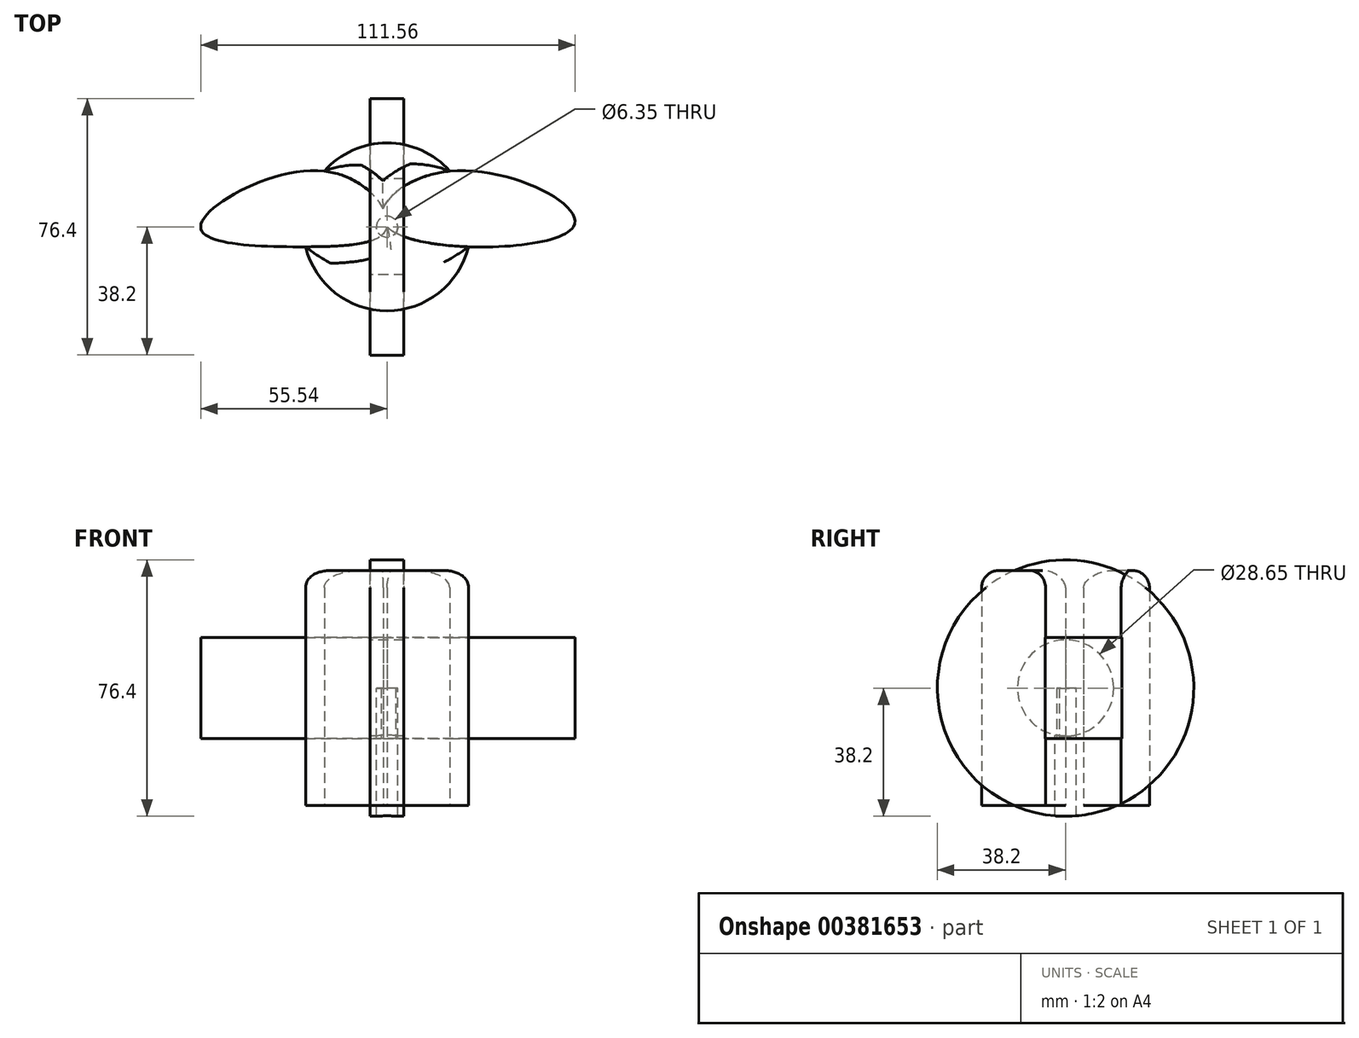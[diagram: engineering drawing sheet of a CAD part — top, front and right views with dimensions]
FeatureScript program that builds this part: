
annotation { "Feature Type Name" : "Feature", "Feature Type Description" : "" }
export const myFeature = defineFeature(function(context is Context, id is Id, definition is map)
    precondition{}
    {
        {
            var Q0;
            Q0=qCreatedBy(makeId("Top.planeOp"),FACE);
            var sketch = newSketch(context, id + "F0", { "sketchPlane" : qUnion([Q0])});
            skCircle(sketch, "E0", {"center": v(0, 0) * mm, "radius": 25 * mm});
            skFitSpline(sketch, "E1", {"points": [v(18.7, 16.58) * mm, v(55.54, 0) * mm, v(0, 0) * mm, v(18.7, 16.58) * mm]});
            skLineSegment(sketch, "E2", {"start": v(25, 0) * mm, "end": v(55.54, 0) * mm});
            skLineSegment(sketch, "E3", {"start": v(-25, 0) * mm, "end": v(-55.54, 0) * mm});
            skLineSegment(sketch, "E4", {"start": v(24.28, -5.95) * mm, "end": v(-24.28, -5.95) * mm});
            skFitSpline(sketch, "E5", {"points": [v(-18.7, 16.58) * mm, v(-55.54, 0) * mm, v(-24.28, -5.95) * mm, v(0, 0) * mm, v(-18.7, 16.58) * mm]});
            skSolve(sketch);
        }
        {
            var Q0;
            {var subQ0=sQuery(id+"F0.wireOp",EDGE,"E1");var subQ1=sQuery(id+"F0.wireOp",EDGE,"E0");var subQ2=makeQuery(id+"F0.imprint","INTERSECT",VERTEX,{"derivedFrom":[subQ1,subQ0]});Q0=makeQuery(id+"F0.imprint","IMPRINT",FACE,{"disambiguationData":[TD([[makeQuery(id+"F0.imprint","IMPRINT",EDGE,{"disambiguationData":[TD([[subQ2,-1.0]])],"derivedFrom":subQ1}),1.0]])]});}
            var Q1;
            {var subQ0=sQuery(id+"F0.wireOp",EDGE,"E4");Q1=makeQuery(id+"F0.imprint","IMPRINT",FACE,{"disambiguationData":[TD([[makeQuery(id+"F0.imprint","IMPRINT",EDGE,{"derivedFrom":subQ0}),1.0]])]});}
            var Q2;
            {var subQ0=sQuery(id+"F0.wireOp",EDGE,"E4");Q2=makeQuery(id+"F0.imprint","IMPRINT",FACE,{"disambiguationData":[TD([[makeQuery(id+"F0.imprint","IMPRINT",EDGE,{"derivedFrom":subQ0}),-1.0]])]});}
            extrude(context, id + "F1", {"entities" : qUnion([Q0, Q1, Q2]), "endBound" : BoundingType.SYMMETRIC, "depth" : 70 * mm});
        }
        {
            var Q0;
            {var subQ0=sQuery(id+"F0.wireOp",EDGE,"E3");Q0=makeQuery(id+"F0.imprint","IMPRINT",FACE,{"disambiguationData":[TD([[makeQuery(id+"F0.imprint","IMPRINT",EDGE,{"derivedFrom":subQ0}),-1.0]])]});}
            var Q1;
            {var subQ1=sQuery(id+"F0.wireOp",EDGE,"E0");var subQ6=makeQuery(id+"F0.imprint","INTERSECT",VERTEX,{"derivedFrom":[subQ1,sQuery(id+"F0.wireOp",EDGE,"E3")]});Q1=makeQuery(id+"F0.imprint","IMPRINT",FACE,{"disambiguationData":[TD([[makeQuery(id+"F0.imprint","IMPRINT",EDGE,{"disambiguationData":[TD([[subQ6,1.0]])],"derivedFrom":subQ1}),1.0]])]});}
            var Q2;
            {var subQ0=sQuery(id+"F0.wireOp",EDGE,"E3");Q2=makeQuery(id+"F0.imprint","IMPRINT",FACE,{"disambiguationData":[TD([[makeQuery(id+"F0.imprint","IMPRINT",EDGE,{"derivedFrom":subQ0}),1.0]])]});}
            var Q3;
            {var subQ0=sQuery(id+"F0.wireOp",EDGE,"E2");Q3=makeQuery(id+"F0.imprint","IMPRINT",FACE,{"disambiguationData":[TD([[makeQuery(id+"F0.imprint","IMPRINT",EDGE,{"derivedFrom":subQ0}),1.0]])]});}
            var Q4;
            {var subQ1=sQuery(id+"F0.wireOp",EDGE,"E0");var subQ7=makeQuery(id+"F0.imprint","INTERSECT",VERTEX,{"derivedFrom":[subQ1,sQuery(id+"F0.wireOp",EDGE,"E2")]});Q4=makeQuery(id+"F0.imprint","IMPRINT",FACE,{"disambiguationData":[TD([[makeQuery(id+"F0.imprint","IMPRINT",EDGE,{"disambiguationData":[TD([[subQ7,-1.0]])],"derivedFrom":subQ1}),1.0]])]});}
            var Q5;
            {var subQ0=sQuery(id+"F0.wireOp",EDGE,"E2");Q5=makeQuery(id+"F0.imprint","IMPRINT",FACE,{"disambiguationData":[TD([[makeQuery(id+"F0.imprint","IMPRINT",EDGE,{"derivedFrom":subQ0}),-1.0]])]});}
            var Q6;
            {var subQ0=sQuery(id+"F0.wireOp",EDGE,"E5");var subQ1=sQuery(id+"F0.wireOp",EDGE,"E1");var subQ2=makeQuery(id+"F0.imprint","INTERSECT",VERTEX,{"disambiguationData":[OD(0.0)],"derivedFrom":[subQ1,subQ0]});Q6=makeQuery(id+"F0.imprint","IMPRINT",FACE,{"disambiguationData":[TD([[makeQuery(id+"F0.imprint","IMPRINT",EDGE,{"disambiguationData":[TD([[subQ2,-1.0]])],"derivedFrom":subQ1}),-1.0]])]});}
            extrude(context, id + "F2", {"entities" : qUnion([Q0, Q1, Q2, Q3, Q4, Q5, Q6]), "endBound" : BoundingType.SYMMETRIC, "depth" : 30 * mm});
        }
        {
            var Q0;
            {var subQ0=sQuery(id+"F0.wireOp",EDGE,"E5");Q0=makeQuery(id+"F1.opExtrude","CAP_EDGE",EDGE,{"disambiguationData":[OSD([subQ0]),TDD([makeQuery(id+"F0.imprint","IMPRINT",EDGE,{"disambiguationData":[TD([[makeQuery(id+"F0.imprint","INTERSECT",VERTEX,{"disambiguationData":[OD(0.0)],"derivedFrom":[sQuery(id+"F0.wireOp",EDGE,"E1"),subQ0]}),1.0]])],"derivedFrom":subQ0})])],"isStart":false});}
            var Q1;
            {var subQ0=sQuery(id+"F0.wireOp",EDGE,"E1");Q1=makeQuery(id+"F1.opExtrude","CAP_EDGE",EDGE,{"disambiguationData":[OSD([subQ0]),TDD([makeQuery(id+"F0.imprint","IMPRINT",EDGE,{"disambiguationData":[TD([[makeQuery(id+"F0.imprint","INTERSECT",VERTEX,{"disambiguationData":[OD(0.0)],"derivedFrom":[subQ0,sQuery(id+"F0.wireOp",EDGE,"E5")]}),1.0]])],"derivedFrom":subQ0})])],"isStart":false});}
            var Q2;
            {var subQ0=sQuery(id+"F0.wireOp",EDGE,"E1");Q2=makeQuery(id+"F1.opExtrude","CAP_EDGE",EDGE,{"disambiguationData":[OSD([subQ0]),TDD([makeQuery(id+"F0.imprint","IMPRINT",EDGE,{"disambiguationData":[TD([[makeQuery(id+"F0.imprint","INTERSECT",VERTEX,{"derivedFrom":[sQuery(id+"F0.wireOp",EDGE,"E0"),subQ0]}),1.0]])],"derivedFrom":subQ0})])],"isStart":false});}
            var Q3;
            {var subQ0=sQuery(id+"F0.wireOp",EDGE,"E5");Q3=makeQuery(id+"F1.opExtrude","CAP_EDGE",EDGE,{"disambiguationData":[OSD([subQ0]),TDD([makeQuery(id+"F0.imprint","IMPRINT",EDGE,{"disambiguationData":[TD([[makeQuery(id+"F0.imprint","INTERSECT",VERTEX,{"derivedFrom":[sQuery(id+"F0.wireOp",EDGE,"E0"),subQ0]}),1.0]])],"derivedFrom":subQ0})])],"isStart":false});}
            var Q4;
            {var subQ0=sQuery(id+"F0.wireOp",EDGE,"E4");var subQ1=sQuery(id+"F0.wireOp",EDGE,"E0");Q4=makeQuery(id+"F1.opExtrude","CAP_EDGE",EDGE,{"disambiguationData":[OSD([subQ1]),TDD([makeQuery(id+"F0.imprint","IMPRINT",EDGE,{"disambiguationData":[TD([[makeQuery(id+"F0.imprint","INTERSECT",VERTEX,{"derivedFrom":[subQ1,sQuery(id+"F0.wireOp",EDGE,"E1"),subQ0]}),1.0]])],"derivedFrom":subQ1})])],"isStart":false});}
            var Q5;
            {var subQ0=sQuery(id+"F0.wireOp",EDGE,"E0");Q5=makeQuery(id+"F1.opExtrude","CAP_EDGE",EDGE,{"disambiguationData":[OSD([subQ0]),TDD([makeQuery(id+"F0.imprint","IMPRINT",EDGE,{"disambiguationData":[TD([[makeQuery(id+"F0.imprint","INTERSECT",VERTEX,{"derivedFrom":[subQ0,sQuery(id+"F0.wireOp",EDGE,"E1")]}),-1.0]])],"derivedFrom":subQ0})])],"isStart":false});}
            fillet(context, id + "F3", {"entities" : qUnion([Q0, Q1, Q2, Q3, Q4, Q5]), "radius" : 5.08 * mm, "tangentPropagation" : true, "allowEdgeOverflow" : false});
        }
        {
            var Q0;
            Q0=qCreatedBy(makeId("Right.planeOp"),FACE);
            var sketch = newSketch(context, id + "F4", { "sketchPlane" : qUnion([Q0])});
            skCircle(sketch, "E6", {"center": v(0, 0) * mm, "radius": 14.32 * mm});
            skCircle(sketch, "E7", {"center": v(0, 0) * mm, "radius": 38.2 * mm});
            skSolve(sketch);
        }
        {
            var Q0;
            Q0=makeQuery(id+"F4.imprint","IMPRINT",FACE,{"disambiguationData":[TD([[makeQuery(id+"F4.imprint","IMPRINT",EDGE,{"derivedFrom":sQuery(id+"F4.wireOp",EDGE,"E6")}),-1.0]])]});
            extrude(context, id + "F5", {"entities" : qUnion([Q0]), "endBound" : BoundingType.SYMMETRIC, "depth" : 10 * mm});
        }
        {
            var Q0;
            Q0=sQuery(id+"F0.wireOp",VERTEX,"E5.3.internal");
            var Q1;
            Q1=makeQuery(id+"F2.opExtrude","SWEPT_BODY",BODY,{"disambiguationData":[OSD([sQuery(id+"F0.wireOp",EDGE,"E1"),sQuery(id+"F0.wireOp",EDGE,"E5")])]});
            var Q2;
            Q2=makeQuery(id+"F5.opExtrude","SWEPT_BODY",BODY,{"disambiguationData":[OSD([sQuery(id+"F4.wireOp",EDGE,"E6"),sQuery(id+"F4.wireOp",EDGE,"E7")])]});
            hole(context, id + "F6", {"style" : HoleStyle.SIMPLE, "endStyle" : HoleEndStyle.THROUGH, "holeDiameter" : 6.35 * mm, "isTappedThrough" : true, "tappedDepth" : 12.7 * mm, "tapClearance" : 3, "locations" : qUnion([Q0]), "scope" : qUnion([Q1, Q2])});
        }
    });
